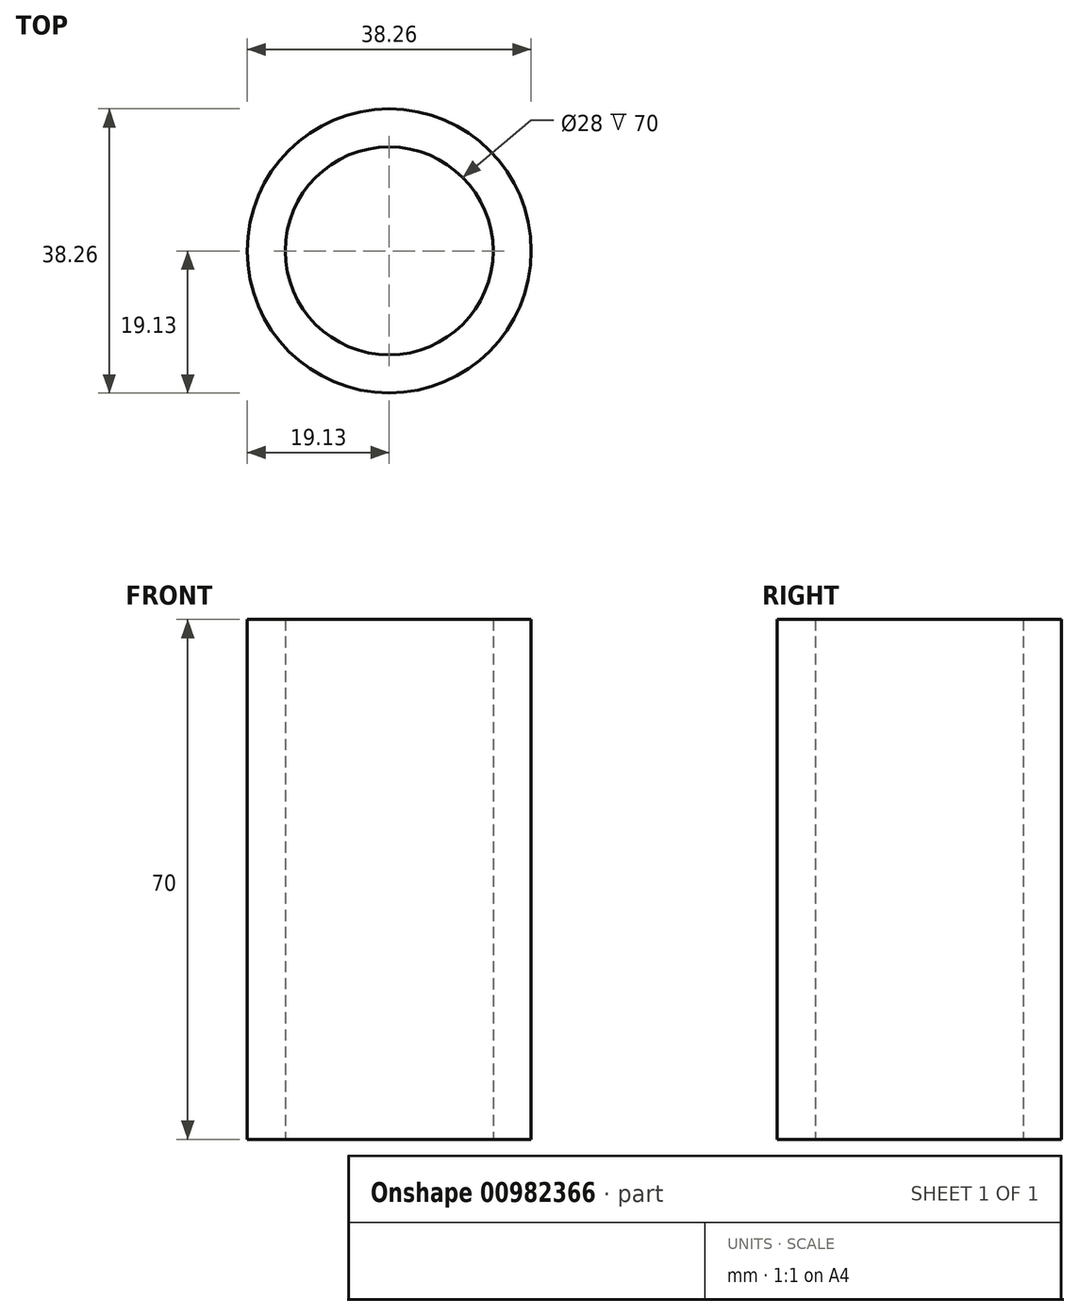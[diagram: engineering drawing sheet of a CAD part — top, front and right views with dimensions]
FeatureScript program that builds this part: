
annotation { "Feature Type Name" : "Feature", "Feature Type Description" : "" }
export const myFeature = defineFeature(function(context is Context, id is Id, definition is map)
    precondition{}
    {
        {
            var Q0;
            Q0=qCreatedBy(makeId("Top.planeOp"),FACE);
            var sketch = newSketch(context, id + "F0", { "sketchPlane" : qUnion([Q0])});
            skCircle(sketch, "E0", {"center": v(0, 0) * mm, "radius": 19.12 * mm});
            skCircle(sketch, "E1", {"center": v(0, 0) * mm, "radius": 14 * mm});
            skSolve(sketch);
        }
        {
            var Q0;
            Q0=makeQuery(id+"F0.imprint","IMPRINT",FACE,{"disambiguationData":[TD([[makeQuery(id+"F0.imprint","IMPRINT",EDGE,{"derivedFrom":sQuery(id+"F0.wireOp",EDGE,"E0")}),1.0]])]});
            extrude(context, id + "F1", {"entities" : qUnion([Q0]), "flatOperationType" : FlatOperationType.REMOVE, "depth" : 70 * mm, "offsetDistance" : 25 * mm, "domain" : OperationDomain.MODEL});
        }
    });
